# Revit family: Котел_ТЕРМОТЕХНИК_ТТ100_1-20 мВт
name_source: partatom
category: Оборудование
units: mm (PartAtom-declared; Revit-internal decimal feet)

## family parameters
Всегда вертикально = Да
Классификация = Нет
На основе рабочей плоскости = Нет
Общий = Нет
При загрузке вырезать с полостями = Нет
Размер круглого соединителя = Использовать диаметр
Тип детали = Нормальный
Точка расчета площади = Нет

## types (23) — shared parameters
G = 25 мм
URL = https://www.entroros.ru
Видимость_ВКЛ = Да
Видимость_ВЫКЛ = Нет
Изготовитель = ЭНТРОРОС
КПД (%) не менее = 94
Ключевая пометка = https://www.entroros.ru
Код по классификатору = D3020100
Материал_Условный BOX = <По категории>
Описание = Котел ЭНТРОРОС ТЕРМОТЕХНИК ТТ100
Производитель = ЭНТРОРОС
Семейство заказано = ООО ЭНТРОРОС (entroros.ru)
Семейство оборудования = ТТ100
Семейство разработано = ООО DASBIM (dasbim.ru)
Ссылка на документацию = https://www.entroros.ru
Штуцер_Датчик дым.газов_D = G1/2-B
Штуцер_Датчик темп. воды на входе_D = G1/2-B
Штуцер_Датчик темп. воды на выходе_D = G1/2-B
Штуцер_Люк смотровой_D = 225х160
Штуцер_Слив конденсата_D = 25 мм
Штуцер_Слив конденсата_D_Формула = G1-B
Штуцер_Тягонапоромер_D = G1/2-B
zero-valued in all types: Стоимость

## per-type parameters (varying)
- 01_1000_ef_206: B=1540 мм; H=1768 мм; L=3180 мм; А_Дверь_Смещение наружной грани=3038 мм; Аэродин. сопротивление (Па)=238; Дверь_051=Нет; Дверь_052=Нет; Дверь_053=Нет; Дверь_054=Нет; Дверь_055=Нет; Дверь_056=Нет; Дверь_206=Да; Дверь_208=Нет; Дверь_210=Нет; Дверь_212=Нет; Дверь_213=Нет; Комментарии к типоразмеру=1.0 мВт; Корпус_051=Нет; Корпус_052=Нет; Корпус_053=Нет; Корпус_054=Нет; Корпус_055=Нет; Корпус_056=Нет; Корпус_206=Да; Корпус_208=Нет; Корпус_209=Нет; Корпус_210=Нет; Корпус_211=Нет; Корпус_212=Нет; Корпус_213=Нет; Масса (кг)=3170; Ном. мощность (кВт)=1000; Подключение горелки=300; С_Ось котла=910 мм; Штуцер_Вход воды_D=125 мм; Штуцер_Вход воды_А=400 мм; Штуцер_Выход воды_D=125 мм; Штуцер_Выход воды_А=1038 мм; Штуцер_Выход дыма_D=350 мм; Штуцер_Выход дыма_В=1360 мм; Штуцер_Люк смотровой_А=300 мм; Штуцер_Подключение горелки=300 мм; Штуцер_Пред.клапан1_D=50 мм; Штуцер_Пред.клапан1_А=730 мм; Штуцер_Пред.клапан2_D=50 мм; Штуцер_Пред.клапан2_а=0 мм; Штуцер_Слив воды_D=40 мм; Штуцер_Слив воды_D_Формула=G1/2-B; Штуцер_Слив воды_А=11 мм; Штуцер_Слив воды_В=89 мм; Штуцер_Слив конденсата_А=14 мм; Штуцер_Слив конденсата_В=230 мм
- 02_1500_ef_207: B=1540 мм; H=1768 мм; L=3180 мм; А_Дверь_Смещение наружной грани=3038 мм; Аэродин. сопротивление (Па)=627; Дверь_051=Нет; Дверь_052=Нет; Дверь_053=Нет; Дверь_054=Нет; Дверь_055=Нет; Дверь_056=Нет; Дверь_206=Да; Дверь_208=Нет; Дверь_210=Нет; Дверь_212=Нет; Дверь_213=Нет; Комментарии к типоразмеру=1.5 мВт; Корпус_051=Нет; Корпус_052=Нет; Корпус_053=Нет; Корпус_054=Нет; Корпус_055=Нет; Корпус_056=Нет; Корпус_206=Да; Корпус_208=Нет; Корпус_209=Нет; Корпус_210=Нет; Корпус_211=Нет; Корпус_212=Нет; Корпус_213=Нет; Масса (кг)=3303; Ном. мощность (кВт)=1500; Подключение горелки=300; С_Ось котла=910 мм; Штуцер_Вход воды_D=125 мм; Штуцер_Вход воды_А=400 мм; Штуцер_Выход воды_D=125 мм; Штуцер_Выход воды_А=1038 мм; Штуцер_Выход дыма_D=350 мм; Штуцер_Выход дыма_В=1360 мм; Штуцер_Люк смотровой_А=300 мм; Штуцер_Подключение горелки=300 мм; Штуцер_Пред.клапан1_D=50 мм; Штуцер_Пред.клапан1_А=730 мм; Штуцер_Пред.клапан2_D=50 мм; Штуцер_Пред.клапан2_а=0 мм; Штуцер_Слив воды_D=40 мм; Штуцер_Слив воды_D_Формула=G1/2-B; Штуцер_Слив воды_А=11 мм; Штуцер_Слив воды_В=89 мм; Штуцер_Слив конденсата_А=14 мм; Штуцер_Слив конденсата_В=230 мм
- 03_2000_ef_208: B=1740 мм; H=1968 мм; L=3485 мм; А_Дверь_Смещение наружной грани=3340 мм; Аэродин. сопротивление (Па)=774; Дверь_051=Нет; Дверь_052=Нет; Дверь_053=Нет; Дверь_054=Нет; Дверь_055=Нет; Дверь_056=Нет; Дверь_206=Нет; Дверь_208=Да; Дверь_210=Нет; Дверь_212=Нет; Дверь_213=Нет; Комментарии к типоразмеру=2.0 мВт; Корпус_051=Нет; Корпус_052=Нет; Корпус_053=Нет; Корпус_054=Нет; Корпус_055=Нет; Корпус_056=Нет; Корпус_206=Нет; Корпус_208=Да; Корпус_209=Нет; Корпус_210=Нет; Корпус_211=Нет; Корпус_212=Нет; Корпус_213=Нет; Масса (кг)=4410; Ном. мощность (кВт)=2000; Подключение горелки=380; С_Ось котла=1010 мм; Штуцер_Вход воды_D=150 мм; Штуцер_Вход воды_А=550 мм; Штуцер_Выход воды_D=150 мм; Штуцер_Выход воды_А=820 мм; Штуцер_Выход дыма_D=500 мм; Штуцер_Выход дыма_В=1520 мм; Штуцер_Люк смотровой_А=855 мм; Штуцер_Подключение горелки=380 мм; Штуцер_Пред.клапан1_D=65 мм; Штуцер_Пред.клапан1_А=1205 мм; Штуцер_Пред.клапан2_D=65 мм; Штуцер_Пред.клапан2_а=300 мм; Штуцер_Слив воды_D=40 мм; Штуцер_Слив воды_D_Формула=G1/2-B; Штуцер_Слив воды_А=0 мм; Штуцер_Слив воды_В=89 мм; Штуцер_Слив конденсата_А=12 мм; Штуцер_Слив конденсата_В=232 мм
- 04_2200_ef_2081: B=1740 мм; H=1968 мм; L=3485 мм; А_Дверь_Смещение наружной грани=3340 мм; Аэродин. сопротивление (Па)=972; Дверь_051=Нет; Дверь_052=Нет; Дверь_053=Нет; Дверь_054=Нет; Дверь_055=Нет; Дверь_056=Нет; Дверь_206=Нет; Дверь_208=Да; Дверь_210=Нет; Дверь_212=Нет; Дверь_213=Нет; Комментарии к типоразмеру=2.2 мВт; Корпус_051=Нет; Корпус_052=Нет; Корпус_053=Нет; Корпус_054=Нет; Корпус_055=Нет; Корпус_056=Нет; Корпус_206=Нет; Корпус_208=Да; Корпус_209=Нет; Корпус_210=Нет; Корпус_211=Нет; Корпус_212=Нет; Корпус_213=Нет; Масса (кг)=4589; Ном. мощность (кВт)=2200; Подключение горелки=380; С_Ось котла=1010 мм; Штуцер_Вход воды_D=150 мм; Штуцер_Вход воды_А=550 мм; Штуцер_Выход воды_D=150 мм; Штуцер_Выход воды_А=820 мм; Штуцер_Выход дыма_D=500 мм; Штуцер_Выход дыма_В=1520 мм; Штуцер_Люк смотровой_А=855 мм; Штуцер_Подключение горелки=380 мм; Штуцер_Пред.клапан1_D=65 мм; Штуцер_Пред.клапан1_А=1205 мм; Штуцер_Пред.клапан2_D=65 мм; Штуцер_Пред.клапан2_а=300 мм; Штуцер_Слив воды_D=40 мм; Штуцер_Слив воды_D_Формула=G1/2-B; Штуцер_Слив воды_А=0 мм; Штуцер_Слив воды_В=89 мм; Штуцер_Слив конденсата_А=12 мм; Штуцер_Слив конденсата_В=232 мм
- 05_2500_ef_209: B=1740 мм; H=1968 мм; L=3735 мм; А_Дверь_Смещение наружной грани=3590 мм; Аэродин. сопротивление (Па)=964; Дверь_051=Нет; Дверь_052=Нет; Дверь_053=Нет; Дверь_054=Нет; Дверь_055=Нет; Дверь_056=Нет; Дверь_206=Нет; Дверь_208=Да; Дверь_210=Нет; Дверь_212=Нет; Дверь_213=Нет; Комментарии к типоразмеру=2.5 мВт; Корпус_051=Нет; Корпус_052=Нет; Корпус_053=Нет; Корпус_054=Нет; Корпус_055=Нет; Корпус_056=Нет; Корпус_206=Нет; Корпус_208=Нет; Корпус_209=Да; Корпус_210=Нет; Корпус_211=Нет; Корпус_212=Нет; Корпус_213=Нет; Масса (кг)=5016; Ном. мощность (кВт)=2500; Подключение горелки=380; С_Ось котла=1010 мм; Штуцер_Вход воды_D=150 мм; Штуцер_Вход воды_А=550 мм; Штуцер_Выход воды_D=150 мм; Штуцер_Выход воды_А=875 мм; Штуцер_Выход дыма_D=500 мм; Штуцер_Выход дыма_В=1520 мм; Штуцер_Люк смотровой_А=1000 мм; Штуцер_Подключение горелки=380 мм; Штуцер_Пред.клапан1_D=65 мм; Штуцер_Пред.клапан1_А=1400 мм; Штуцер_Пред.клапан2_D=65 мм; Штуцер_Пред.клапан2_а=300 мм; Штуцер_Слив воды_D=40 мм; Штуцер_Слив воды_D_Формула=G1/2-B; Штуцер_Слив воды_А=0 мм; Штуцер_Слив воды_В=89 мм; Штуцер_Слив конденсата_А=12 мм; Штуцер_Слив конденсата_В=232 мм
- 06_3000_ef_210: B=1940 мм; H=2168 мм; L=4125 мм; А_Дверь_Смещение наружной грани=3976 мм; Аэродин. сопротивление (Па)=833; Дверь_051=Нет; Дверь_052=Нет; Дверь_053=Нет; Дверь_054=Нет; Дверь_055=Нет; Дверь_056=Нет; Дверь_206=Нет; Дверь_208=Нет; Дверь_210=Да; Дверь_212=Нет; Дверь_213=Нет; Комментарии к типоразмеру=3.0 мВт; Корпус_051=Нет; Корпус_052=Нет; Корпус_053=Нет; Корпус_054=Нет; Корпус_055=Нет; Корпус_056=Нет; Корпус_206=Нет; Корпус_208=Нет; Корпус_209=Нет; Корпус_210=Да; Корпус_211=Нет; Корпус_212=Нет; Корпус_213=Нет; Масса (кг)=6427; Ном. мощность (кВт)=3000; Подключение горелки=450; С_Ось котла=1110 мм; Штуцер_Вход воды_D=200 мм; Штуцер_Вход воды_А=600 мм; Штуцер_Выход воды_D=200 мм; Штуцер_Выход воды_А=961 мм; Штуцер_Выход дыма_D=500 мм; Штуцер_Выход дыма_В=1720 мм; Штуцер_Люк смотровой_А=1200 мм; Штуцер_Подключение горелки=450 мм; Штуцер_Пред.клапан1_D=65 мм; Штуцер_Пред.клапан1_А=1600 мм; Штуцер_Пред.клапан2_D=65 мм; Штуцер_Пред.клапан2_а=300 мм; Штуцер_Слив воды_D=40 мм; Штуцер_Слив воды_D_Формула=G1/2-B; Штуцер_Слив воды_А=0 мм; Штуцер_Слив воды_В=89 мм; Штуцер_Слив конденсата_А=14 мм; Штуцер_Слив конденсата_В=235 мм
- 07_3200_ef_2101: B=1940 мм; H=2168 мм; L=4125 мм; А_Дверь_Смещение наружной грани=3976 мм; Аэродин. сопротивление (Па)=974; Дверь_051=Нет; Дверь_052=Нет; Дверь_053=Нет; Дверь_054=Нет; Дверь_055=Нет; Дверь_056=Нет; Дверь_206=Нет; Дверь_208=Нет; Дверь_210=Да; Дверь_212=Нет; Дверь_213=Нет; Комментарии к типоразмеру=3.2 мВт; Корпус_051=Нет; Корпус_052=Нет; Корпус_053=Нет; Корпус_054=Нет; Корпус_055=Нет; Корпус_056=Нет; Корпус_206=Нет; Корпус_208=Нет; Корпус_209=Нет; Корпус_210=Да; Корпус_211=Нет; Корпус_212=Нет; Корпус_213=Нет; Масса (кг)=6695; Ном. мощность (кВт)=3200; Подключение горелки=450; С_Ось котла=1110 мм; Штуцер_Вход воды_D=200 мм; Штуцер_Вход воды_А=600 мм; Штуцер_Выход воды_D=200 мм; Штуцер_Выход воды_А=961 мм; Штуцер_Выход дыма_D=500 мм; Штуцер_Выход дыма_В=1720 мм; Штуцер_Люк смотровой_А=1200 мм; Штуцер_Подключение горелки=450 мм; Штуцер_Пред.клапан1_D=65 мм; Штуцер_Пред.клапан1_А=1600 мм; Штуцер_Пред.клапан2_D=65 мм; Штуцер_Пред.клапан2_а=300 мм; Штуцер_Слив воды_D=40 мм; Штуцер_Слив воды_D_Формула=G1/2-B; Штуцер_Слив воды_А=0 мм; Штуцер_Слив воды_В=89 мм; Штуцер_Слив конденсата_А=14 мм; Штуцер_Слив конденсата_В=235 мм
- 08_3500_ef_211: B=1940 мм; H=2168 мм; L=4528 мм; А_Дверь_Смещение наружной грани=4376 мм; Аэродин. сопротивление (Па)=1153; Дверь_051=Нет; Дверь_052=Нет; Дверь_053=Нет; Дверь_054=Нет; Дверь_055=Нет; Дверь_056=Нет; Дверь_206=Нет; Дверь_208=Нет; Дверь_210=Да; Дверь_212=Нет; Дверь_213=Нет; Комментарии к типоразмеру=3.5 мВт; Корпус_051=Нет; Корпус_052=Нет; Корпус_053=Нет; Корпус_054=Нет; Корпус_055=Нет; Корпус_056=Нет; Корпус_206=Нет; Корпус_208=Нет; Корпус_209=Нет; Корпус_210=Нет; Корпус_211=Да; Корпус_212=Нет; Корпус_213=Нет; Масса (кг)=7294; Ном. мощность (кВт)=3500; Подключение горелки=450; С_Ось котла=1110 мм; Штуцер_Вход воды_D=200 мм; Штуцер_Вход воды_А=600 мм; Штуцер_Выход воды_D=200 мм; Штуцер_Выход воды_А=1011 мм; Штуцер_Выход дыма_D=500 мм; Штуцер_Выход дыма_В=1720 мм; Штуцер_Люк смотровой_А=1550 мм; Штуцер_Подключение горелки=450 мм; Штуцер_Пред.клапан1_D=65 мм; Штуцер_Пред.клапан1_А=1950 мм; Штуцер_Пред.клапан2_D=65 мм; Штуцер_Пред.клапан2_а=300 мм; Штуцер_Слив воды_D=40 мм; Штуцер_Слив воды_D_Формула=G1/2-B; Штуцер_Слив воды_А=0 мм; Штуцер_Слив воды_В=89 мм; Штуцер_Слив конденсата_А=14 мм; Штуцер_Слив конденсата_В=233 мм
- 09_4200_ef_212: B=2100 мм; H=2328 мм; L=4819 мм; А_Дверь_Смещение наружной грани=4674 мм; Аэродин. сопротивление (Па)=1125; Дверь_051=Нет; Дверь_052=Нет; Дверь_053=Нет; Дверь_054=Нет; Дверь_055=Нет; Дверь_056=Нет; Дверь_206=Нет; Дверь_208=Нет; Дверь_210=Нет; Дверь_212=Да; Дверь_213=Нет; Комментарии к типоразмеру=4.2 мВт; Корпус_051=Нет; Корпус_052=Нет; Корпус_053=Нет; Корпус_054=Нет; Корпус_055=Нет; Корпус_056=Нет; Корпус_206=Нет; Корпус_208=Нет; Корпус_209=Нет; Корпус_210=Нет; Корпус_211=Нет; Корпус_212=Да; Корпус_213=Нет; Масса (кг)=8777; Ном. мощность (кВт)=4200; Подключение горелки=450; С_Ось котла=1205 мм; Штуцер_Вход воды_D=200 мм; Штуцер_Вход воды_А=700 мм; Штуцер_Выход воды_D=200 мм; Штуцер_Выход воды_А=959 мм; Штуцер_Выход дыма_D=650 мм; Штуцер_Выход дыма_В=1805 мм; Штуцер_Люк смотровой_А=1400 мм; Штуцер_Подключение горелки=450 мм; Штуцер_Пред.клапан1_D=80 мм; Штуцер_Пред.клапан1_А=2100 мм; Штуцер_Пред.клапан2_D=80 мм; Штуцер_Пред.клапан2_а=300 мм; Штуцер_Слив воды_D=40 мм; Штуцер_Слив воды_D_Формула=G1/2-B; Штуцер_Слив воды_А=0 мм; Штуцер_Слив воды_В=119 мм; Штуцер_Слив конденсата_А=12 мм; Штуцер_Слив конденсата_В=266 мм
- 10_5000_ef_2121: B=2100 мм; H=2328 мм; L=4819 мм; А_Дверь_Смещение наружной грани=4674 мм; Аэродин. сопротивление (Па)=1679; Дверь_051=Нет; Дверь_052=Нет; Дверь_053=Нет; Дверь_054=Нет; Дверь_055=Нет; Дверь_056=Нет; Дверь_206=Нет; Дверь_208=Нет; Дверь_210=Нет; Дверь_212=Да; Дверь_213=Нет; Комментарии к типоразмеру=5.0 мВт; Корпус_051=Нет; Корпус_052=Нет; Корпус_053=Нет; Корпус_054=Нет; Корпус_055=Нет; Корпус_056=Нет; Корпус_206=Нет; Корпус_208=Нет; Корпус_209=Нет; Корпус_210=Нет; Корпус_211=Нет; Корпус_212=Да; Корпус_213=Нет; Масса (кг)=9145; Ном. мощность (кВт)=5000; Подключение горелки=450; С_Ось котла=1205 мм; Штуцер_Вход воды_D=200 мм; Штуцер_Вход воды_А=700 мм; Штуцер_Выход воды_D=200 мм; Штуцер_Выход воды_А=959 мм; Штуцер_Выход дыма_D=650 мм; Штуцер_Выход дыма_В=1805 мм; Штуцер_Люк смотровой_А=1400 мм; Штуцер_Подключение горелки=450 мм; Штуцер_Пред.клапан1_D=80 мм; Штуцер_Пред.клапан1_А=2100 мм; Штуцер_Пред.клапан2_D=80 мм; Штуцер_Пред.клапан2_а=300 мм; Штуцер_Слив воды_D=40 мм; Штуцер_Слив воды_D_Формула=G1/2-B; Штуцер_Слив воды_А=0 мм; Штуцер_Слив воды_В=119 мм; Штуцер_Слив конденсата_А=12 мм; Штуцер_Слив конденсата_В=266 мм
- 11_5400_ef_213: B=2200 мм; H=2438 мм; L=5104 мм; А_Дверь_Смещение наружной грани=4960 мм; Аэродин. сопротивление (Па)=983; Дверь_051=Нет; Дверь_052=Нет; Дверь_053=Нет; Дверь_054=Нет; Дверь_055=Нет; Дверь_056=Нет; Дверь_206=Нет; Дверь_208=Нет; Дверь_210=Нет; Дверь_212=Нет; Дверь_213=Да; Комментарии к типоразмеру=5.4 мВт; Корпус_051=Нет; Корпус_052=Нет; Корпус_053=Нет; Корпус_054=Нет; Корпус_055=Нет; Корпус_056=Нет; Корпус_206=Нет; Корпус_208=Нет; Корпус_209=Нет; Корпус_210=Нет; Корпус_211=Нет; Корпус_212=Нет; Корпус_213=Да; Масса (кг)=10395; Ном. мощность (кВт)=5400; Подключение горелки=450; С_Ось котла=1258 мм; Штуцер_Вход воды_D=250 мм; Штуцер_Вход воды_А=800 мм; Штуцер_Выход воды_D=250 мм; Штуцер_Выход воды_А=1143 мм; Штуцер_Выход дыма_D=650 мм; Штуцер_Выход дыма_В=1886 мм; Штуцер_Люк смотровой_А=1400 мм; Штуцер_Подключение горелки=450 мм; Штуцер_Пред.клапан1_D=80 мм; Штуцер_Пред.клапан1_А=2100 мм; Штуцер_Пред.клапан2_D=80 мм; Штуцер_Пред.клапан2_а=300 мм; Штуцер_Слив воды_D=50 мм; Штуцер_Слив воды_D_Формула=50; Штуцер_Слив воды_А=0 мм; Штуцер_Слив воды_В=135 мм; Штуцер_Слив конденсата_А=12 мм; Штуцер_Слив конденсата_В=259 мм
- 12_6000_ef_2131: B=2200 мм; H=2438 мм; L=5104 мм; А_Дверь_Смещение наружной грани=4960 мм; Аэродин. сопротивление (Па)=1258; Дверь_051=Нет; Дверь_052=Нет; Дверь_053=Нет; Дверь_054=Нет; Дверь_055=Нет; Дверь_056=Нет; Дверь_206=Нет; Дверь_208=Нет; Дверь_210=Нет; Дверь_212=Нет; Дверь_213=Да; Комментарии к типоразмеру=6.0 мВт; Корпус_051=Нет; Корпус_052=Нет; Корпус_053=Нет; Корпус_054=Нет; Корпус_055=Нет; Корпус_056=Нет; Корпус_206=Нет; Корпус_208=Нет; Корпус_209=Нет; Корпус_210=Нет; Корпус_211=Нет; Корпус_212=Нет; Корпус_213=Да; Масса (кг)=10829; Ном. мощность (кВт)=6000; Подключение горелки=450; С_Ось котла=1258 мм; Штуцер_Вход воды_D=250 мм; Штуцер_Вход воды_А=800 мм; Штуцер_Выход воды_D=250 мм; Штуцер_Выход воды_А=1143 мм; Штуцер_Выход дыма_D=650 мм; Штуцер_Выход дыма_В=1886 мм; Штуцер_Люк смотровой_А=1400 мм; Штуцер_Подключение горелки=450 мм; Штуцер_Пред.клапан1_D=80 мм; Штуцер_Пред.клапан1_А=2100 мм; Штуцер_Пред.клапан2_D=80 мм; Штуцер_Пред.клапан2_а=300 мм; Штуцер_Слив воды_D=50 мм; Штуцер_Слив воды_D_Формула=50; Штуцер_Слив воды_А=0 мм; Штуцер_Слив воды_В=135 мм; Штуцер_Слив конденсата_А=12 мм; Штуцер_Слив конденсата_В=259 мм
- 13_6500_ef_051: B=2360 мм; H=2574 мм; L=5402 мм; А_Дверь_Смещение наружной грани=5249 мм; Аэродин. сопротивление (Па)=1046; Дверь_051=Да; Дверь_052=Нет; Дверь_053=Нет; Дверь_054=Нет; Дверь_055=Нет; Дверь_056=Нет; Дверь_206=Нет; Дверь_208=Нет; Дверь_210=Нет; Дверь_212=Нет; Дверь_213=Нет; Комментарии к типоразмеру=6.5 мВт; Корпус_051=Да; Корпус_052=Нет; Корпус_053=Нет; Корпус_054=Нет; Корпус_055=Нет; Корпус_056=Нет; Корпус_206=Нет; Корпус_208=Нет; Корпус_209=Нет; Корпус_210=Нет; Корпус_211=Нет; Корпус_212=Нет; Корпус_213=Нет; Масса (кг)=12948; Ном. мощность (кВт)=6500; Подключение горелки=500; С_Ось котла=1314 мм; Штуцер_Вход воды_D=250 мм; Штуцер_Вход воды_А=900 мм; Штуцер_Выход воды_D=250 мм; Штуцер_Выход воды_А=1134 мм; Штуцер_Выход дыма_D=800 мм; Штуцер_Выход дыма_В=1970 мм; Штуцер_Люк смотровой_А=1500 мм; Штуцер_Подключение горелки=500 мм; Штуцер_Пред.клапан1_D=100 мм; Штуцер_Пред.клапан1_А=1970 мм; Штуцер_Пред.клапан2_D=100 мм; Штуцер_Пред.клапан2_а=470 мм; Штуцер_Слив воды_D=50 мм; Штуцер_Слив воды_D_Формула=50; Штуцер_Слив воды_А=4 мм; Штуцер_Слив воды_В=109 мм; Штуцер_Слив конденсата_А=3 мм; Штуцер_Слив конденсата_В=237 мм
- 14_7000_ef_0511: B=2360 мм; H=2574 мм; L=5402 мм; А_Дверь_Смещение наружной грани=5249 мм; Аэродин. сопротивление (Па)=1245; Дверь_051=Да; Дверь_052=Нет; Дверь_053=Нет; Дверь_054=Нет; Дверь_055=Нет; Дверь_056=Нет; Дверь_206=Нет; Дверь_208=Нет; Дверь_210=Нет; Дверь_212=Нет; Дверь_213=Нет; Комментарии к типоразмеру=7.0 мВт; Корпус_051=Да; Корпус_052=Нет; Корпус_053=Нет; Корпус_054=Нет; Корпус_055=Нет; Корпус_056=Нет; Корпус_206=Нет; Корпус_208=Нет; Корпус_209=Нет; Корпус_210=Нет; Корпус_211=Нет; Корпус_212=Нет; Корпус_213=Нет; Масса (кг)=13491; Ном. мощность (кВт)=7000; Подключение горелки=500; С_Ось котла=1314 мм; Штуцер_Вход воды_D=250 мм; Штуцер_Вход воды_А=900 мм; Штуцер_Выход воды_D=250 мм; Штуцер_Выход воды_А=1134 мм; Штуцер_Выход дыма_D=800 мм; Штуцер_Выход дыма_В=1970 мм; Штуцер_Люк смотровой_А=1500 мм; Штуцер_Подключение горелки=500 мм; Штуцер_Пред.клапан1_D=100 мм; Штуцер_Пред.клапан1_А=1970 мм; Штуцер_Пред.клапан2_D=100 мм; Штуцер_Пред.клапан2_а=470 мм; Штуцер_Слив воды_D=50 мм; Штуцер_Слив воды_D_Формула=50; Штуцер_Слив воды_А=4 мм; Штуцер_Слив воды_В=109 мм; Штуцер_Слив конденсата_А=3 мм; Штуцер_Слив конденсата_В=237 мм
- 15_8000_ef_052: B=2500 мм; H=2710 мм; L=5808 мм; А_Дверь_Смещение наружной грани=5651 мм; Аэродин. сопротивление (Па)=1161; Дверь_051=Нет; Дверь_052=Да; Дверь_053=Нет; Дверь_054=Нет; Дверь_055=Нет; Дверь_056=Нет; Дверь_206=Нет; Дверь_208=Нет; Дверь_210=Нет; Дверь_212=Нет; Дверь_213=Нет; Комментарии к типоразмеру=8.0 мВт; Корпус_051=Нет; Корпус_052=Да; Корпус_053=Нет; Корпус_054=Нет; Корпус_055=Нет; Корпус_056=Нет; Корпус_206=Нет; Корпус_208=Нет; Корпус_209=Нет; Корпус_210=Нет; Корпус_211=Нет; Корпус_212=Нет; Корпус_213=Нет; Масса (кг)=15720; Ном. мощность (кВт)=8000; Подключение горелки=590; С_Ось котла=1370 мм; Штуцер_Вход воды_D=300 мм; Штуцер_Вход воды_А=1000 мм; Штуцер_Выход воды_D=300 мм; Штуцер_Выход воды_А=1218 мм; Штуцер_Выход дыма_D=800 мм; Штуцер_Выход дыма_В=2070 мм; Штуцер_Люк смотровой_А=1500 мм; Штуцер_Подключение горелки=590 мм; Штуцер_Пред.клапан1_D=100 мм; Штуцер_Пред.клапан1_А=1990 мм; Штуцер_Пред.клапан2_D=100 мм; Штуцер_Пред.клапан2_а=500 мм; Штуцер_Слив воды_D=50 мм; Штуцер_Слив воды_D_Формула=50; Штуцер_Слив воды_А=0 мм; Штуцер_Слив воды_В=95 мм; Штуцер_Слив конденсата_А=3 мм; Штуцер_Слив конденсата_В=213 мм
- 16_8700_ef_0521: B=2500 мм; H=2710 мм; L=5808 мм; А_Дверь_Смещение наружной грани=5651 мм; Аэродин. сопротивление (Па)=1415; Дверь_051=Нет; Дверь_052=Да; Дверь_053=Нет; Дверь_054=Нет; Дверь_055=Нет; Дверь_056=Нет; Дверь_206=Нет; Дверь_208=Нет; Дверь_210=Нет; Дверь_212=Нет; Дверь_213=Нет; Комментарии к типоразмеру=8.7 мВт; Корпус_051=Нет; Корпус_052=Да; Корпус_053=Нет; Корпус_054=Нет; Корпус_055=Нет; Корпус_056=Нет; Корпус_206=Нет; Корпус_208=Нет; Корпус_209=Нет; Корпус_210=Нет; Корпус_211=Нет; Корпус_212=Нет; Корпус_213=Нет; Масса (кг)=16373; Ном. мощность (кВт)=8700; Подключение горелки=590; С_Ось котла=1370 мм; Штуцер_Вход воды_D=300 мм; Штуцер_Вход воды_А=1000 мм; Штуцер_Выход воды_D=300 мм; Штуцер_Выход воды_А=1218 мм; Штуцер_Выход дыма_D=800 мм; Штуцер_Выход дыма_В=2070 мм; Штуцер_Люк смотровой_А=1500 мм; Штуцер_Подключение горелки=590 мм; Штуцер_Пред.клапан1_D=100 мм; Штуцер_Пред.клапан1_А=1990 мм; Штуцер_Пред.клапан2_D=100 мм; Штуцер_Пред.клапан2_а=500 мм; Штуцер_Слив воды_D=50 мм; Штуцер_Слив воды_D_Формула=50; Штуцер_Слив воды_А=0 мм; Штуцер_Слив воды_В=95 мм; Штуцер_Слив конденсата_А=3 мм; Штуцер_Слив конденсата_В=213 мм
- 17_10000_ef_053: B=2680 мм; H=2900 мм; L=6443 мм; А_Дверь_Смещение наружной грани=6296 мм; Аэродин. сопротивление (Па)=1351; Дверь_051=Нет; Дверь_052=Нет; Дверь_053=Да; Дверь_054=Нет; Дверь_055=Нет; Дверь_056=Нет; Дверь_206=Нет; Дверь_208=Нет; Дверь_210=Нет; Дверь_212=Нет; Дверь_213=Нет; Комментарии к типоразмеру=10.0 мВт; Корпус_051=Нет; Корпус_052=Нет; Корпус_053=Да; Корпус_054=Нет; Корпус_055=Нет; Корпус_056=Нет; Корпус_206=Нет; Корпус_208=Нет; Корпус_209=Нет; Корпус_210=Нет; Корпус_211=Нет; Корпус_212=Нет; Корпус_213=Нет; Масса (кг)=18851; Ном. мощность (кВт)=10000; Подключение горелки=590; С_Ось котла=1490 мм; Штуцер_Вход воды_D=300 мм; Штуцер_Вход воды_А=1400 мм; Штуцер_Выход воды_D=300 мм; Штуцер_Выход воды_А=1228 мм; Штуцер_Выход дыма_D=900 мм; Штуцер_Выход дыма_В=2130 мм; Штуцер_Люк смотровой_А=1850 мм; Штуцер_Подключение горелки=590 мм; Штуцер_Пред.клапан1_D=125 мм; Штуцер_Пред.клапан1_А=2350 мм; Штуцер_Пред.клапан2_D=125 мм; Штуцер_Пред.клапан2_а=500 мм; Штуцер_Слив воды_D=50 мм; Штуцер_Слив воды_D_Формула=50; Штуцер_Слив воды_А=23 мм; Штуцер_Слив воды_В=135 мм; Штуцер_Слив конденсата_А=25 мм; Штуцер_Слив конденсата_В=261 мм
- 18_12000_ef_054: B=2860 мм; H=3074 мм; L=6948 мм; А_Дверь_Смещение наружной грани=6801 мм; Аэродин. сопротивление (Па)=1388; Дверь_051=Нет; Дверь_052=Нет; Дверь_053=Нет; Дверь_054=Да; Дверь_055=Нет; Дверь_056=Нет; Дверь_206=Нет; Дверь_208=Нет; Дверь_210=Нет; Дверь_212=Нет; Дверь_213=Нет; Комментарии к типоразмеру=12.0 мВт; Корпус_051=Нет; Корпус_052=Нет; Корпус_053=Нет; Корпус_054=Да; Корпус_055=Нет; Корпус_056=Нет; Корпус_206=Нет; Корпус_208=Нет; Корпус_209=Нет; Корпус_210=Нет; Корпус_211=Нет; Корпус_212=Нет; Корпус_213=Нет; Масса (кг)=20728; Ном. мощность (кВт)=12000; Подключение горелки=730; С_Ось котла=1564 мм; Штуцер_Вход воды_D=350 мм; Штуцер_Вход воды_А=1600 мм; Штуцер_Выход воды_D=350 мм; Штуцер_Выход воды_А=1506 мм; Штуцер_Выход дыма_D=1000 мм; Штуцер_Выход дыма_В=2364 мм; Штуцер_Люк смотровой_А=2000 мм; Штуцер_Подключение горелки=730 мм; Штуцер_Пред.клапан1_D=125 мм; Штуцер_Пред.клапан1_А=2440 мм; Штуцер_Пред.клапан2_D=125 мм; Штуцер_Пред.клапан2_а=500 мм; Штуцер_Слив воды_D=50 мм; Штуцер_Слив воды_D_Формула=50; Штуцер_Слив воды_А=0 мм; Штуцер_Слив воды_В=109 мм; Штуцер_Слив конденсата_А=94 мм; Штуцер_Слив конденсата_В=237 мм
- 19_13000_ef_0541: B=2860 мм; H=3074 мм; L=6948 мм; А_Дверь_Смещение наружной грани=6801 мм; Аэродин. сопротивление (Па)=1678; Дверь_051=Нет; Дверь_052=Нет; Дверь_053=Нет; Дверь_054=Да; Дверь_055=Нет; Дверь_056=Нет; Дверь_206=Нет; Дверь_208=Нет; Дверь_210=Нет; Дверь_212=Нет; Дверь_213=Нет; Комментарии к типоразмеру=13.0 мВт; Корпус_051=Нет; Корпус_052=Нет; Корпус_053=Нет; Корпус_054=Да; Корпус_055=Нет; Корпус_056=Нет; Корпус_206=Нет; Корпус_208=Нет; Корпус_209=Нет; Корпус_210=Нет; Корпус_211=Нет; Корпус_212=Нет; Корпус_213=Нет; Масса (кг)=21589; Ном. мощность (кВт)=13000; Подключение горелки=730; С_Ось котла=1564 мм; Штуцер_Вход воды_D=350 мм; Штуцер_Вход воды_А=1600 мм; Штуцер_Выход воды_D=350 мм; Штуцер_Выход воды_А=1506 мм; Штуцер_Выход дыма_D=1000 мм; Штуцер_Выход дыма_В=2364 мм; Штуцер_Люк смотровой_А=2000 мм; Штуцер_Подключение горелки=730 мм; Штуцер_Пред.клапан1_D=125 мм; Штуцер_Пред.клапан1_А=2440 мм; Штуцер_Пред.клапан2_D=125 мм; Штуцер_Пред.клапан2_а=500 мм; Штуцер_Слив воды_D=50 мм; Штуцер_Слив воды_D_Формула=50; Штуцер_Слив воды_А=0 мм; Штуцер_Слив воды_В=109 мм; Штуцер_Слив конденсата_А=94 мм; Штуцер_Слив конденсата_В=237 мм
- 20_15000_ef_055: B=3060 мм; H=3276 мм; L=7608 мм; А_Дверь_Смещение наружной грани=7461 мм; Аэродин. сопротивление (Па)=1669; Дверь_051=Нет; Дверь_052=Нет; Дверь_053=Нет; Дверь_054=Нет; Дверь_055=Да; Дверь_056=Нет; Дверь_206=Нет; Дверь_208=Нет; Дверь_210=Нет; Дверь_212=Нет; Дверь_213=Нет; Комментарии к типоразмеру=15.0 мВт; Корпус_051=Нет; Корпус_052=Нет; Корпус_053=Нет; Корпус_054=Нет; Корпус_055=Да; Корпус_056=Нет; Корпус_206=Нет; Корпус_208=Нет; Корпус_209=Нет; Корпус_210=Нет; Корпус_211=Нет; Корпус_212=Нет; Корпус_213=Нет; Масса (кг)=26751; Ном. мощность (кВт)=15000; Подключение горелки=730; С_Ось котла=1664 мм; Штуцер_Вход воды_D=400 мм; Штуцер_Вход воды_А=2000 мм; Штуцер_Выход воды_D=400 мм; Штуцер_Выход воды_А=1396 мм; Штуцер_Выход дыма_D=1000 мм; Штуцер_Выход дыма_В=2514 мм; Штуцер_Люк смотровой_А=1700 мм; Штуцер_Подключение горелки=730 мм; Штуцер_Пред.клапан1_D=125 мм; Штуцер_Пред.клапан1_А=2550 мм; Штуцер_Пред.клапан2_D=125 мм; Штуцер_Пред.клапан2_а=600 мм; Штуцер_Слив воды_D=50 мм; Штуцер_Слив воды_D_Формула=50; Штуцер_Слив воды_А=0 мм; Штуцер_Слив воды_В=109 мм; Штуцер_Слив конденсата_А=94 мм; Штуцер_Слив конденсата_В=230 мм
- 21_16500_ef_0551: B=3060 мм; H=3276 мм; L=7608 мм; А_Дверь_Смещение наружной грани=7461 мм; Аэродин. сопротивление (Па)=2087; Дверь_051=Нет; Дверь_052=Нет; Дверь_053=Нет; Дверь_054=Нет; Дверь_055=Да; Дверь_056=Нет; Дверь_206=Нет; Дверь_208=Нет; Дверь_210=Нет; Дверь_212=Нет; Дверь_213=Нет; Комментарии к типоразмеру=16.5 мВт; Корпус_051=Нет; Корпус_052=Нет; Корпус_053=Нет; Корпус_054=Нет; Корпус_055=Да; Корпус_056=Нет; Корпус_206=Нет; Корпус_208=Нет; Корпус_209=Нет; Корпус_210=Нет; Корпус_211=Нет; Корпус_212=Нет; Корпус_213=Нет; Масса (кг)=27866; Ном. мощность (кВт)=16500; Подключение горелки=730; С_Ось котла=1664 мм; Штуцер_Вход воды_D=400 мм; Штуцер_Вход воды_А=2000 мм; Штуцер_Выход воды_D=400 мм; Штуцер_Выход воды_А=1396 мм; Штуцер_Выход дыма_D=1000 мм; Штуцер_Выход дыма_В=2514 мм; Штуцер_Люк смотровой_А=1700 мм; Штуцер_Подключение горелки=730 мм; Штуцер_Пред.клапан1_D=125 мм; Штуцер_Пред.клапан1_А=2550 мм; Штуцер_Пред.клапан2_D=125 мм; Штуцер_Пред.клапан2_а=600 мм; Штуцер_Слив воды_D=50 мм; Штуцер_Слив воды_D_Формула=50; Штуцер_Слив воды_А=0 мм; Штуцер_Слив воды_В=109 мм; Штуцер_Слив конденсата_А=94 мм; Штуцер_Слив конденсата_В=230 мм
- 22_18000_ef_056: B=3390 мм; H=3606 мм; L=8064 мм; А_Дверь_Смещение наружной грани=7920 мм; Аэродин. сопротивление (Па)=1269; Дверь_051=Нет; Дверь_052=Нет; Дверь_053=Нет; Дверь_054=Нет; Дверь_055=Нет; Дверь_056=Да; Дверь_206=Нет; Дверь_208=Нет; Дверь_210=Нет; Дверь_212=Нет; Дверь_213=Нет; Комментарии к типоразмеру=18.0 мВт; Корпус_051=Нет; Корпус_052=Нет; Корпус_053=Нет; Корпус_054=Нет; Корпус_055=Нет; Корпус_056=Да; Корпус_206=Нет; Корпус_208=Нет; Корпус_209=Нет; Корпус_210=Нет; Корпус_211=Нет; Корпус_212=Нет; Корпус_213=Нет; Масса (кг)=38398; Ном. мощность (кВт)=18000; Подключение горелки=740; С_Ось котла=1829 мм; Штуцер_Вход воды_D=400 мм; Штуцер_Вход воды_А=2000 мм; Штуцер_Выход воды_D=400 мм; Штуцер_Выход воды_А=1854 мм; Штуцер_Выход дыма_D=1000 мм; Штуцер_Выход дыма_В=2679 мм; Штуцер_Люк смотровой_А=1700 мм; Штуцер_Подключение горелки=740 мм; Штуцер_Пред.клапан1_D=125 мм; Штуцер_Пред.клапан1_А=2550 мм; Штуцер_Пред.клапан2_D=125 мм; Штуцер_Пред.клапан2_а=600 мм; Штуцер_Слив воды_D=50 мм; Штуцер_Слив воды_D_Формула=50; Штуцер_Слив воды_А=0 мм; Штуцер_Слив воды_В=109 мм; Штуцер_Слив конденсата_А=94 мм; Штуцер_Слив конденсата_В=230 мм
- 23_20000_ef_0561: B=3390 мм; H=3606 мм; L=8064 мм; А_Дверь_Смещение наружной грани=7920 мм; Аэродин. сопротивление (Па)=1614; Дверь_051=Нет; Дверь_052=Нет; Дверь_053=Нет; Дверь_054=Нет; Дверь_055=Нет; Дверь_056=Да; Дверь_206=Нет; Дверь_208=Нет; Дверь_210=Нет; Дверь_212=Нет; Дверь_213=Нет; Комментарии к типоразмеру=20.0 мВт; Корпус_051=Нет; Корпус_052=Нет; Корпус_053=Нет; Корпус_054=Нет; Корпус_055=Нет; Корпус_056=Да; Корпус_206=Нет; Корпус_208=Нет; Корпус_209=Нет; Корпус_210=Нет; Корпус_211=Нет; Корпус_212=Нет; Корпус_213=Нет; Масса (кг)=39998; Ном. мощность (кВт)=20000; Подключение горелки=740; С_Ось котла=1829 мм; Штуцер_Вход воды_D=400 мм; Штуцер_Вход воды_А=2000 мм; Штуцер_Выход воды_D=400 мм; Штуцер_Выход воды_А=1854 мм; Штуцер_Выход дыма_D=1000 мм; Штуцер_Выход дыма_В=2679 мм; Штуцер_Люк смотровой_А=1700 мм; Штуцер_Подключение горелки=740 мм; Штуцер_Пред.клапан1_D=125 мм; Штуцер_Пред.клапан1_А=2550 мм; Штуцер_Пред.клапан2_D=125 мм; Штуцер_Пред.клапан2_а=600 мм; Штуцер_Слив воды_D=50 мм; Штуцер_Слив воды_D_Формула=50; Штуцер_Слив воды_А=0 мм; Штуцер_Слив воды_В=109 мм; Штуцер_Слив конденсата_А=94 мм; Штуцер_Слив конденсата_В=230 мм
